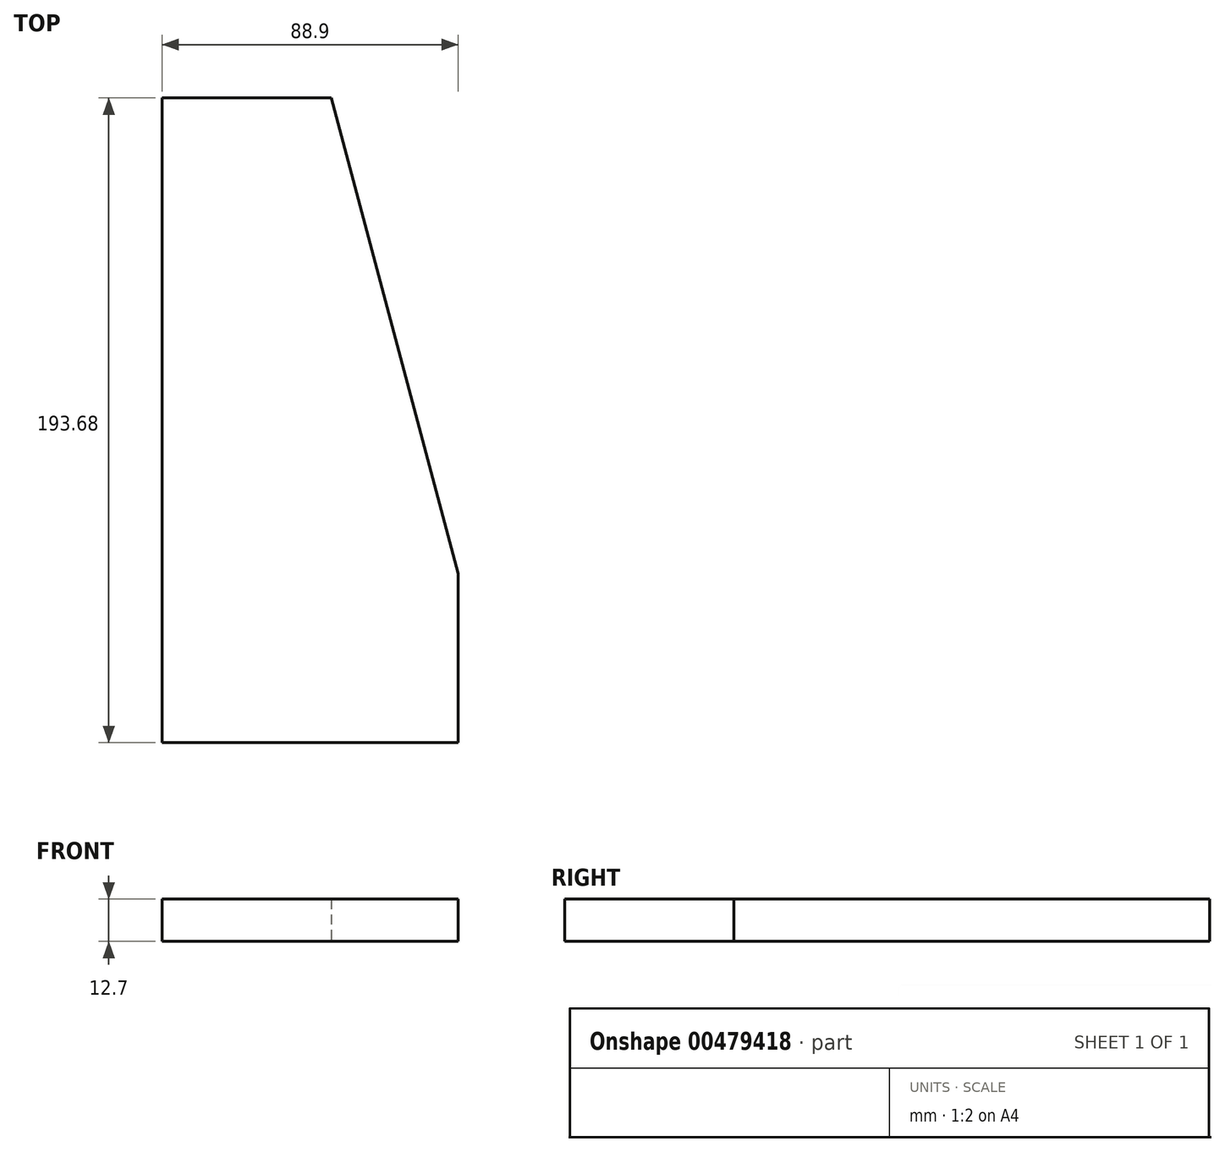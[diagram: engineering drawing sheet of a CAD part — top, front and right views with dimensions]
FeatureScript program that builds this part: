
annotation { "Feature Type Name" : "Feature", "Feature Type Description" : "" }
export const myFeature = defineFeature(function(context is Context, id is Id, definition is map)
    precondition{}
    {
        {
            var Q0;
            Q0=qCreatedBy(makeId("Top.planeOp"),FACE);
            var sketch = newSketch(context, id + "F0", { "sketchPlane" : qUnion([Q0])});
            skLineSegment(sketch, "E0.bottom", {"start": v(0, 0) * mm, "end": v(88.9, 0) * mm});
            skLineSegment(sketch, "E0.top", {"start": v(0, 193.68) * mm, "end": v(88.9, 193.68) * mm});
            skLineSegment(sketch, "E0.left", {"start": v(0, 0) * mm, "end": v(0, 193.68) * mm});
            skLineSegment(sketch, "E0.right", {"start": v(88.9, 0) * mm, "end": v(88.9, 193.68) * mm});
            skLineSegment(sketch, "E1", {"start": v(50.8, 193.68) * mm, "end": v(88.9, 50.8) * mm});
            skSolve(sketch);
        }
        {
            var Q0;
            {var subQ1=sQuery(id+"F0.wireOp",EDGE,"E0.bottom");Q0=makeQuery(id+"F0.imprint","IMPRINT",FACE,{"disambiguationData":[TD([[makeQuery(id+"F0.imprint","IMPRINT",EDGE,{"derivedFrom":subQ1}),1.0]])]});}
            extrude(context, id + "F1", {"entities" : qUnion([Q0]), "depth" : 12.7 * mm, "offsetDistance" : 25.4 * mm});
        }
    });
